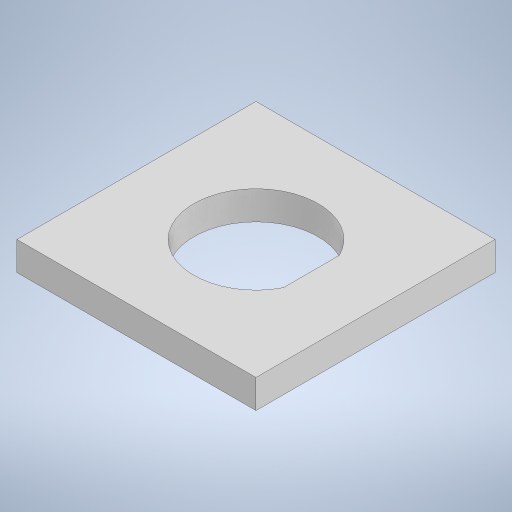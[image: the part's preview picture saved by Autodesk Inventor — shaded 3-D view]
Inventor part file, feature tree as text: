
AUTODESK INVENTOR PART (.ipt)
format: ipt  version: 2024.2 (Build 282272000, 272)  size: 216,576 bytes
history: native  units: mm
features: extrude x1, sketch x1
ambient origin geometry x8: Origin, YZ Plane, XZ Plane, XY Plane, X Axis, Y Axis, Z Axis, Center Point
bodies: Solid1 (feature_tree)
feature tree (2):
  extrude  "Extrusion1"  Depth=25.0mm
  sketch  "Sketch1"  dims[d0=13.0mm d1=25.0mm d2=25.0mm d3=12.5mm d4=12.5mm d5=3.0mm d6=0.0mm d7=5.8mm]
